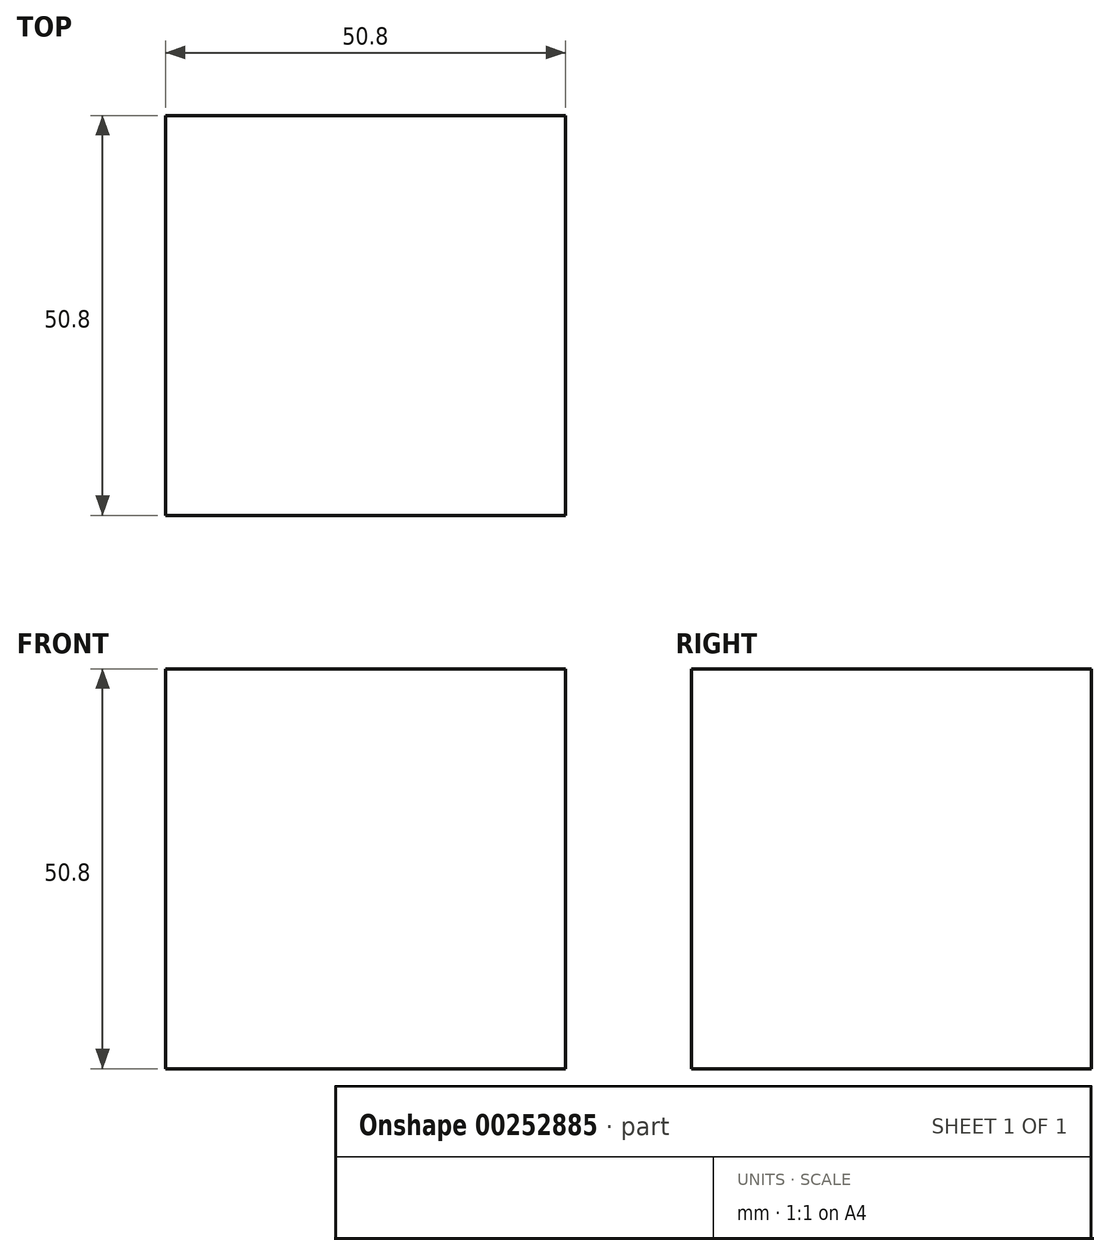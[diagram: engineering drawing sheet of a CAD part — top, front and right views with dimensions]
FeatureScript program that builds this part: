
annotation { "Feature Type Name" : "Feature", "Feature Type Description" : "" }
export const myFeature = defineFeature(function(context is Context, id is Id, definition is map)
    precondition{}
    {
        {
            var Q0;
            Q0=qCreatedBy(makeId("Front.planeOp"),FACE);
            var sketch = newSketch(context, id + "F0", { "sketchPlane" : qUnion([Q0])});
            skLineSegment(sketch, "E0", {"start": v(-25.23, 25.23) * mm, "end": v(25.57, 25.23) * mm});
            skLineSegment(sketch, "E1", {"start": v(25.57, 25.23) * mm, "end": v(25.57, -25.57) * mm});
            skLineSegment(sketch, "E2", {"start": v(25.57, -25.57) * mm, "end": v(-25.23, -25.57) * mm});
            skLineSegment(sketch, "E3", {"start": v(-25.23, -25.57) * mm, "end": v(-25.23, 25.23) * mm});
            skSolve(sketch);
        }
        {
            var Q0;
            Q0=makeQuery(id+"F0.imprint","IMPRINT",FACE,{"disambiguationData":[TD([[makeQuery(id+"F0.imprint","IMPRINT",EDGE,{"derivedFrom":sQuery(id+"F0.wireOp",EDGE,"E0")}),-1.0]])]});
            extrude(context, id + "F1", {"entities" : qUnion([Q0]), "depth" : 50.8 * mm});
        }
    });
